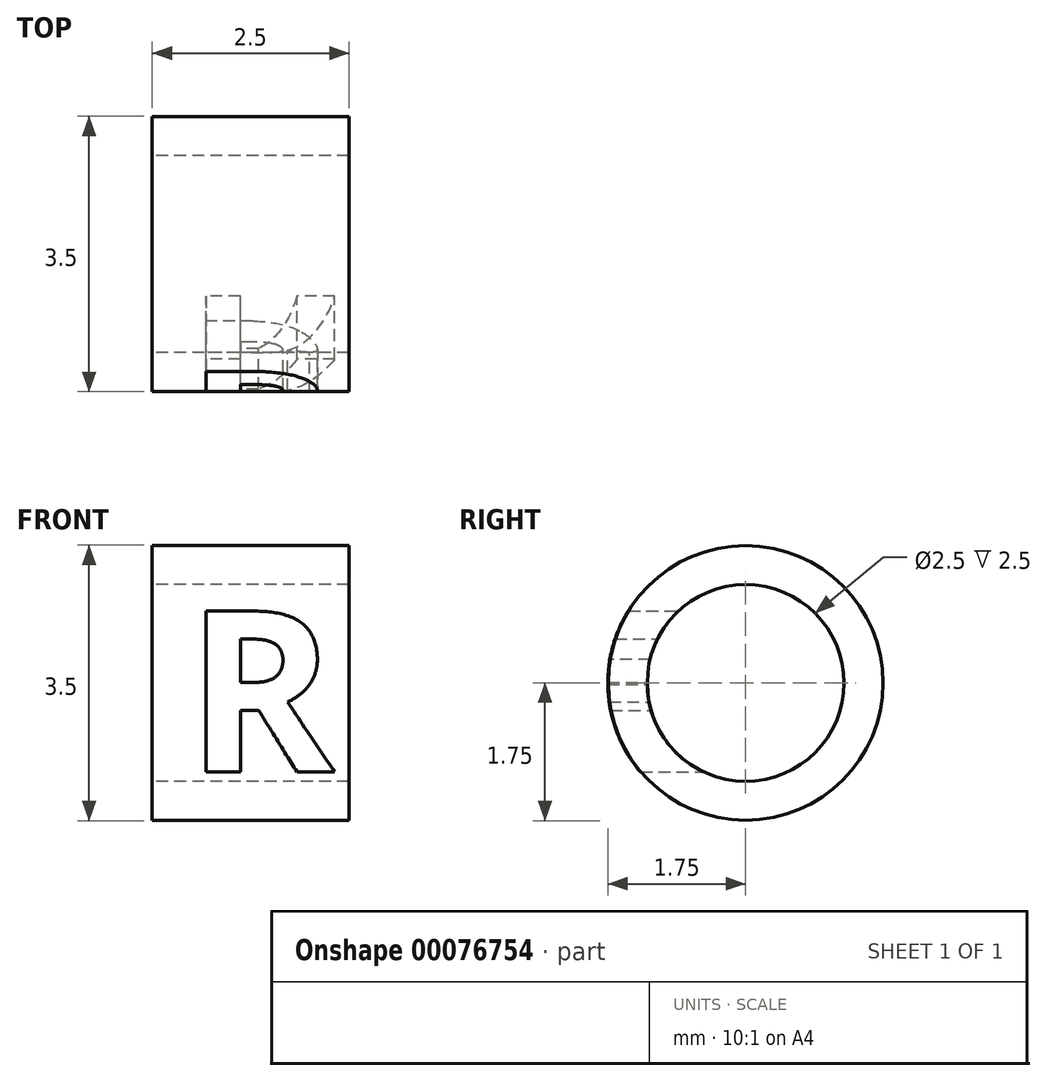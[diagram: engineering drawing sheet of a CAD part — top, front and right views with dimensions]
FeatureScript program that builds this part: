
annotation { "Feature Type Name" : "Feature", "Feature Type Description" : "" }
export const myFeature = defineFeature(function(context is Context, id is Id, definition is map)
    precondition{}
    {
        {
            var Q0;
            Q0=qCreatedBy(makeId("Right.planeOp"),FACE);
            var sketch = newSketch(context, id + "F0", { "sketchPlane" : qUnion([Q0])});
            skCircle(sketch, "E0", {"center": v(0, 0) * mm, "radius": 1.25 * mm});
            skCircle(sketch, "E1", {"center": v(0, 0) * mm, "radius": 1.75 * mm});
            skSolve(sketch);
        }
        {
            var Q0;
            Q0=makeQuery(id+"F0.imprint","IMPRINT",FACE,{"disambiguationData":[TD([[makeQuery(id+"F0.imprint","IMPRINT",EDGE,{"derivedFrom":sQuery(id+"F0.wireOp",EDGE,"E0")}),-1.0]])]});
            var Q1;
            Q1=makeQuery(id+"F0.imprint","IMPRINT",FACE,{"disambiguationData":[TD([[makeQuery(id+"F0.imprint","IMPRINT",EDGE,{"derivedFrom":sQuery(id+"F0.wireOp",EDGE,"E1")}),1.0]])]});
            extrude(context, id + "F1", {"entities" : qUnion([Q0, Q1]), "depth" : 2.5 * mm});
        }
        {
            var Q0;
            Q0=qCreatedBy(makeId("Front.planeOp"),FACE);
            var sketch = newSketch(context, id + "F2", { "sketchPlane" : qUnion([Q0])});
            skText(sketch, "E2", { "text": "R", "fontName": "OpenSans-Bold.ttf"});
            const initialGuessF2  = {"E2": [0.00043, -0.00113, 1, 0, 0.00206]};
            skSetInitialGuess(sketch, initialGuessF2);
            skSolve(sketch);
        }
        {
            var Q0;
            Q0=qSketchRegion(id+"F2",true);
            var Q1;
            Q1=qConstructionFilter(qBodyType(qCreatedBy(id+"F2",EDGE),BodyType.WIRE),ConstructionObject.NO);
            var Q2;
            Q2=makeQuery(id+"F1.opExtrude","SWEPT_FACE",FACE,{"disambiguationData":[OSD([sQuery(id+"F0.wireOp",EDGE,"E1")])]});
            var Q3;
            Q3=makeQuery(id+"F1.opExtrude","SWEPT_BODY",BODY,{"disambiguationData":[OSD([sQuery(id+"F0.wireOp",EDGE,"E0"),sQuery(id+"F0.wireOp",EDGE,"E1")])]});
            var Q4;
            Q4=sQuery(id+"F0.wireOp",VERTEX,"27635d6e-dcd6-4653-b727-4819003c0945");
            extrude(context, id + "F3", {"entities" : qUnion([Q0]), "operationType" : NewBodyOperationType.INTERSECT, "surfaceEntities" : qUnion([Q1]), "endBound" : BoundingType.UP_TO_SURFACE, "endBoundEntityFace" : qUnion([Q2]), "endBoundEntityBody" : qUnion([Q3]), "endBoundEntityVertex" : qUnion([Q4]), "depth" : 25 * mm});
        }
        {
            var Q0;
            Q0=makeQuery(id+"F0.imprint","IMPRINT",FACE,{"disambiguationData":[TD([[makeQuery(id+"F0.imprint","IMPRINT",EDGE,{"derivedFrom":sQuery(id+"F0.wireOp",EDGE,"E0")}),-1.0]])]});
            extrude(context, id + "F4", {"entities" : qUnion([Q0]), "depth" : 2.5 * mm});
        }
    });
